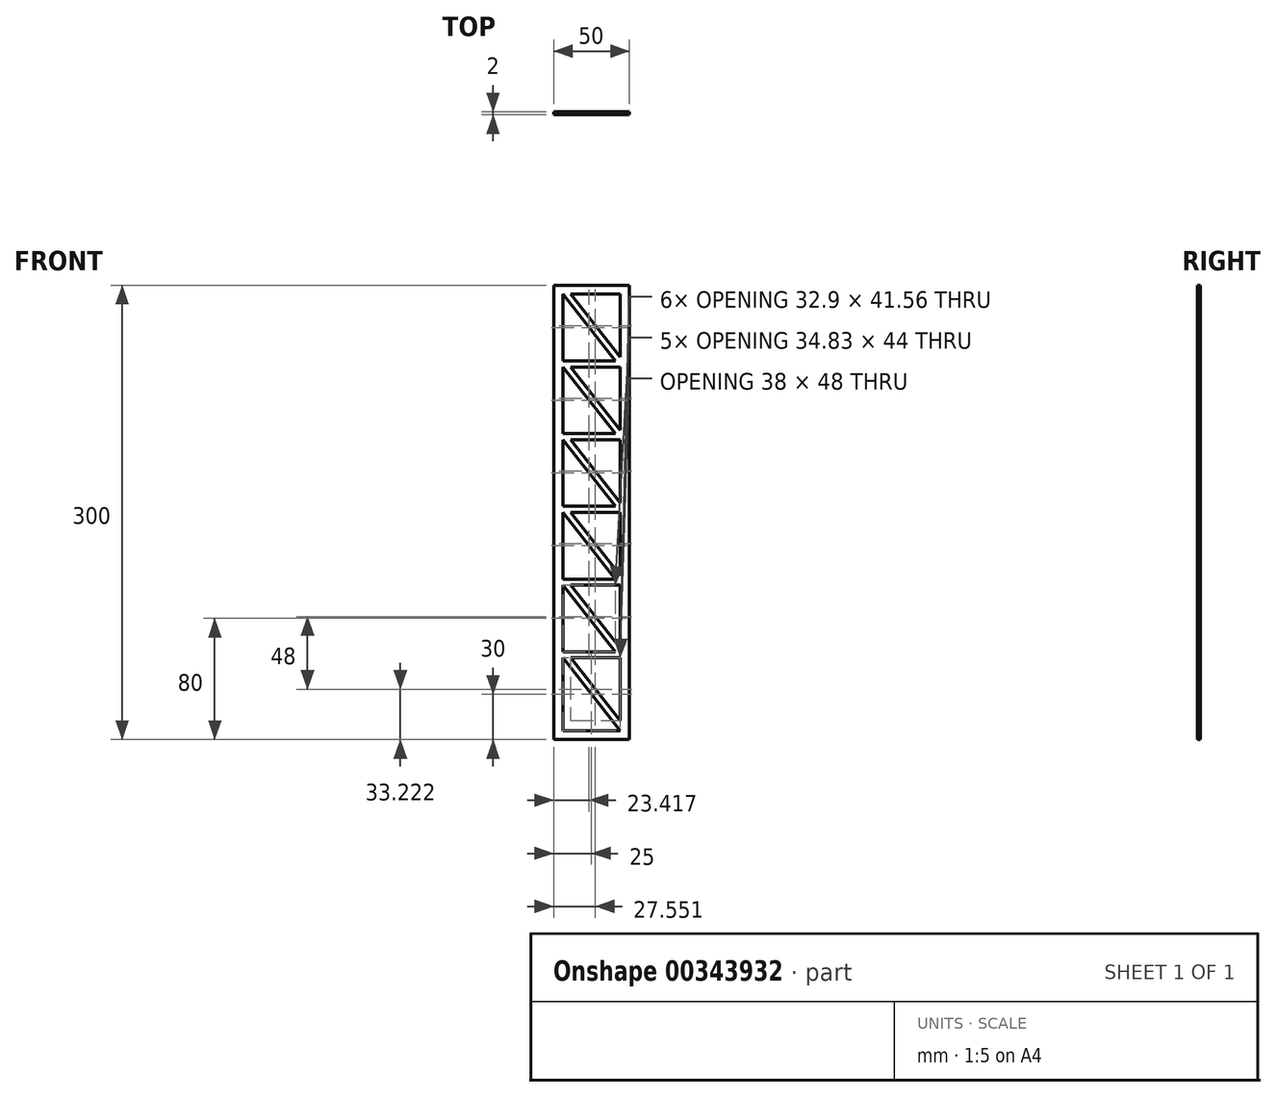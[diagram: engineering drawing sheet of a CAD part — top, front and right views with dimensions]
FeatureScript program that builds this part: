
annotation { "Feature Type Name" : "Feature", "Feature Type Description" : "" }
export const myFeature = defineFeature(function(context is Context, id is Id, definition is map)
    precondition{}
    {
        {
            var Q0;
            Q0=qCreatedBy(makeId("Front.planeOp"),FACE);
            var sketch = newSketch(context, id + "F0", { "sketchPlane" : qUnion([Q0])});
            skLineSegment(sketch, "E0.bottom", {"start": v(0, 0) * mm, "end": v(50, 0) * mm});
            skLineSegment(sketch, "E0.top", {"start": v(0, 300) * mm, "end": v(50, 300) * mm});
            skLineSegment(sketch, "E0.left", {"start": v(0, 0) * mm, "end": v(0, 300) * mm});
            skLineSegment(sketch, "E0.right", {"start": v(50, 0) * mm, "end": v(50, 300) * mm});
            skSolve(sketch);
        }
        {
            var Q0;
            Q0=makeQuery(id+"F0.imprint","IMPRINT",FACE,{"disambiguationData":[TD([[makeQuery(id+"F0.imprint","IMPRINT",EDGE,{"derivedFrom":sQuery(id+"F0.wireOp",EDGE,"E0.bottom")}),1.0]])]});
            var sketch = newSketch(context, id + "F1", { "sketchPlane" : qUnion([Q0])});
            skLineSegment(sketch, "E1.bottom", {"start": v(6, 6) * mm, "end": v(44, 6) * mm});
            skLineSegment(sketch, "E1.top", {"start": v(6, 294) * mm, "end": v(44, 294) * mm});
            skLineSegment(sketch, "E1.left", {"start": v(6, 6) * mm, "end": v(6, 294) * mm});
            skLineSegment(sketch, "E1.right", {"start": v(44, 6) * mm, "end": v(44, 294) * mm});
            skLineSegment(sketch, "E2", {"start": v(6, 294) * mm, "end": v(44, 246) * mm});
            skLineSegment(sketch, "E3", {"start": v(44, 246) * mm, "end": v(6, 246) * mm});
            skLineSegment(sketch, "E4", {"start": v(6, 246) * mm, "end": v(44, 198) * mm});
            skLineSegment(sketch, "E5", {"start": v(44, 198) * mm, "end": v(6, 198) * mm});
            skLineSegment(sketch, "E6", {"start": v(6, 198) * mm, "end": v(44, 150) * mm});
            skLineSegment(sketch, "E7", {"start": v(44, 150) * mm, "end": v(6, 150) * mm});
            skLineSegment(sketch, "E8", {"start": v(6, 150) * mm, "end": v(44, 102) * mm});
            skLineSegment(sketch, "E9", {"start": v(44, 102) * mm, "end": v(6, 102) * mm});
            skLineSegment(sketch, "E10", {"start": v(6, 102) * mm, "end": v(44, 54) * mm});
            skLineSegment(sketch, "E11", {"start": v(44, 54) * mm, "end": v(6, 54) * mm});
            skLineSegment(sketch, "E12", {"start": v(6, 54) * mm, "end": v(44, 6) * mm});
            skLineSegment(sketch, "E13", {"start": v(11.1, 294) * mm, "end": v(44, 252.44) * mm});
            skLineSegment(sketch, "E14", {"start": v(6, 250) * mm, "end": v(40.83, 250) * mm});
            skLineSegment(sketch, "E15", {"start": v(11.1, 246) * mm, "end": v(44, 204.44) * mm});
            skLineSegment(sketch, "E16", {"start": v(6, 202) * mm, "end": v(40.83, 202) * mm});
            skLineSegment(sketch, "E17", {"start": v(11.1, 198) * mm, "end": v(44, 156.44) * mm});
            skLineSegment(sketch, "E18", {"start": v(6, 154) * mm, "end": v(40.83, 154) * mm});
            skLineSegment(sketch, "E19", {"start": v(11.1, 150) * mm, "end": v(44, 108.44) * mm});
            skLineSegment(sketch, "E20", {"start": v(6, 106) * mm, "end": v(40.83, 106) * mm});
            skLineSegment(sketch, "E21", {"start": v(11.1, 102) * mm, "end": v(44, 60.44) * mm});
            skLineSegment(sketch, "E22", {"start": v(6, 58) * mm, "end": v(40.83, 58) * mm});
            skLineSegment(sketch, "E23", {"start": v(11.1, 54) * mm, "end": v(44, 12.44) * mm});
            skLineSegment(sketch, "E24.bottom", {"start": v(0, 0) * mm, "end": v(50, 0) * mm});
            skLineSegment(sketch, "E24.top", {"start": v(0, 300) * mm, "end": v(50, 300) * mm});
            skLineSegment(sketch, "E24.left", {"start": v(0, 0) * mm, "end": v(0, 300) * mm});
            skLineSegment(sketch, "E24.right", {"start": v(50, 0) * mm, "end": v(50, 300) * mm});
            skSolve(sketch);
        }
        {
            var Q0;
            {var subQ18=sQuery(id+"F1.wireOp",EDGE,"E1.bottom");Q0=makeQuery(id+"F1.imprint","IMPRINT",FACE,{"disambiguationData":[TD([[makeQuery(id+"F1.imprint","IMPRINT",EDGE,{"derivedFrom":subQ18}),-1.0]])]});}
            var Q1;
            {var subQ4=sQuery(id+"F1.wireOp",EDGE,"E17");Q1=makeQuery(id+"F1.imprint","IMPRINT",FACE,{"disambiguationData":[TD([[makeQuery(id+"F1.imprint","IMPRINT",EDGE,{"derivedFrom":subQ4}),-1.0]])]});}
            var Q2;
            {var subQ6=sQuery(id+"F1.wireOp",EDGE,"E16");Q2=makeQuery(id+"F1.imprint","IMPRINT",FACE,{"disambiguationData":[TD([[makeQuery(id+"F1.imprint","IMPRINT",EDGE,{"derivedFrom":subQ6}),-1.0]])]});}
            var Q3;
            {var subQ6=sQuery(id+"F1.wireOp",EDGE,"E15");Q3=makeQuery(id+"F1.imprint","IMPRINT",FACE,{"disambiguationData":[TD([[makeQuery(id+"F1.imprint","IMPRINT",EDGE,{"derivedFrom":subQ6}),-1.0]])]});}
            var Q4;
            {var subQ6=sQuery(id+"F1.wireOp",EDGE,"E18");Q4=makeQuery(id+"F1.imprint","IMPRINT",FACE,{"disambiguationData":[TD([[makeQuery(id+"F1.imprint","IMPRINT",EDGE,{"derivedFrom":subQ6}),-1.0]])]});}
            var Q5;
            {var subQ6=sQuery(id+"F1.wireOp",EDGE,"E19");Q5=makeQuery(id+"F1.imprint","IMPRINT",FACE,{"disambiguationData":[TD([[makeQuery(id+"F1.imprint","IMPRINT",EDGE,{"derivedFrom":subQ6}),-1.0]])]});}
            var Q6;
            {var subQ4=sQuery(id+"F1.wireOp",EDGE,"E20");Q6=makeQuery(id+"F1.imprint","IMPRINT",FACE,{"disambiguationData":[TD([[makeQuery(id+"F1.imprint","IMPRINT",EDGE,{"derivedFrom":subQ4}),-1.0]])]});}
            var Q7;
            {var subQ6=sQuery(id+"F1.wireOp",EDGE,"E21");Q7=makeQuery(id+"F1.imprint","IMPRINT",FACE,{"disambiguationData":[TD([[makeQuery(id+"F1.imprint","IMPRINT",EDGE,{"derivedFrom":subQ6}),-1.0]])]});}
            var Q8;
            {var subQ6=sQuery(id+"F1.wireOp",EDGE,"E14");Q8=makeQuery(id+"F1.imprint","IMPRINT",FACE,{"disambiguationData":[TD([[makeQuery(id+"F1.imprint","IMPRINT",EDGE,{"derivedFrom":subQ6}),-1.0]])]});}
            var Q9;
            {var subQ0=sQuery(id+"F1.wireOp",EDGE,"E12");Q9=makeQuery(id+"F1.imprint","IMPRINT",FACE,{"disambiguationData":[TD([[makeQuery(id+"F1.imprint","IMPRINT",EDGE,{"derivedFrom":subQ0}),1.0]])]});}
            var Q10;
            {var subQ4=sQuery(id+"F1.wireOp",EDGE,"E22");Q10=makeQuery(id+"F1.imprint","IMPRINT",FACE,{"disambiguationData":[TD([[makeQuery(id+"F1.imprint","IMPRINT",EDGE,{"derivedFrom":subQ4}),-1.0]])]});}
            var Q11;
            {var subQ4=sQuery(id+"F1.wireOp",EDGE,"E13");Q11=makeQuery(id+"F1.imprint","IMPRINT",FACE,{"disambiguationData":[TD([[makeQuery(id+"F1.imprint","IMPRINT",EDGE,{"derivedFrom":subQ4}),-1.0]])]});}
            extrude(context, id + "F2", {"entities" : qUnion([Q0, Q1, Q2, Q3, Q4, Q5, Q6, Q7, Q8, Q9, Q10, Q11]), "depth" : 2 * mm});
        }
    });
